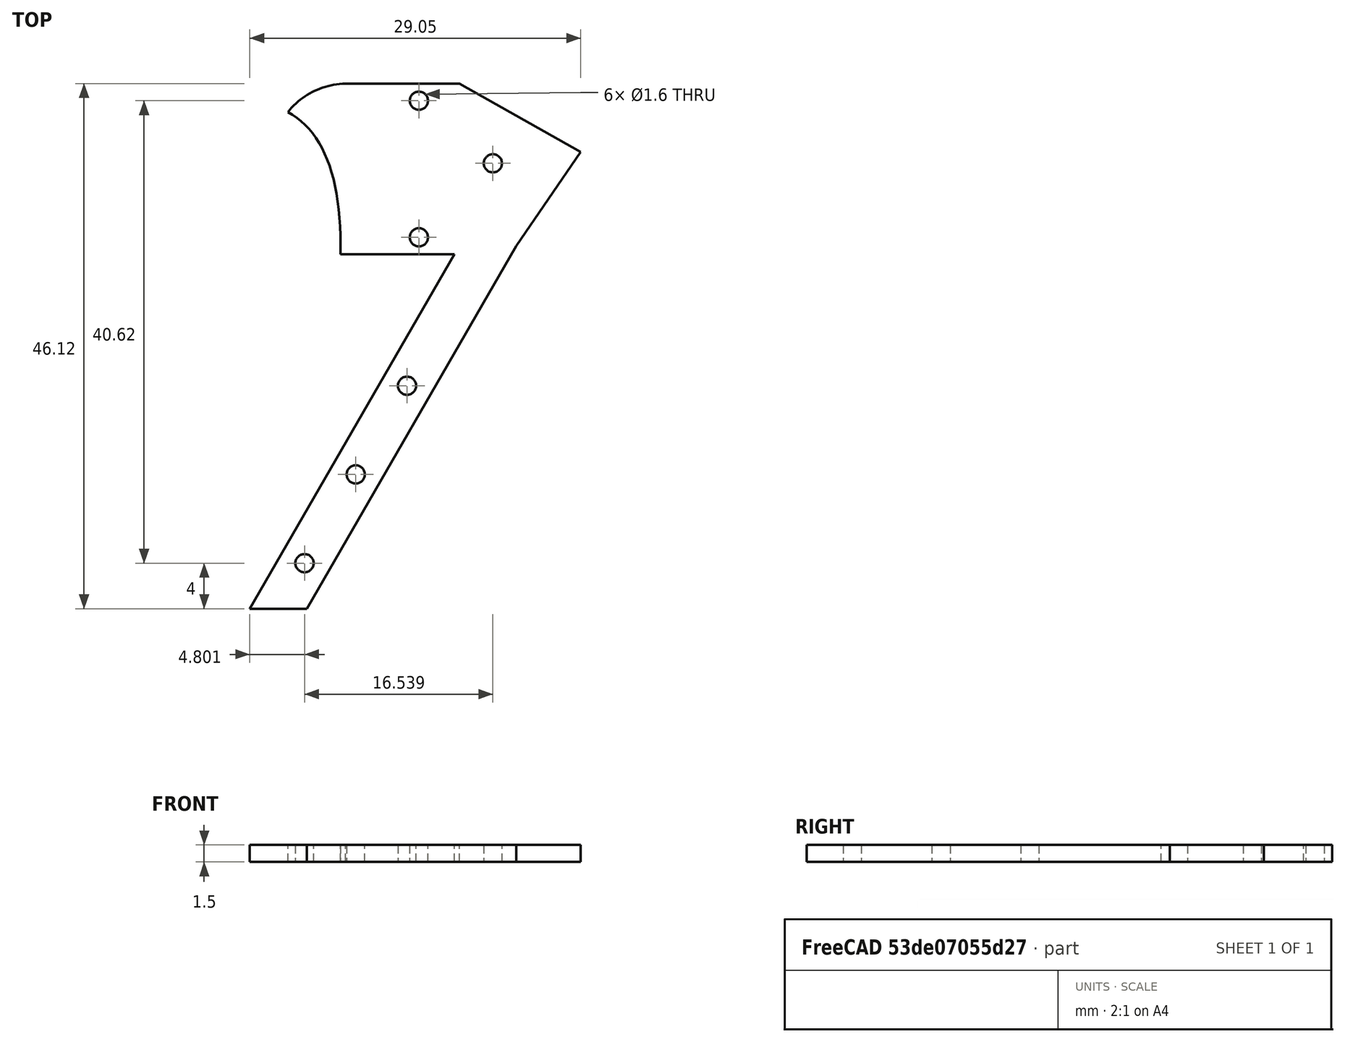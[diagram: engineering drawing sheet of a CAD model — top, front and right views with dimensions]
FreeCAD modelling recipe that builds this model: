
FCSTD DOCUMENT  (FreeCAD 0.17R13519 (Git))
Label: DingDengJia-jwei-2.0
License: All rights reserved
LicenseURL: http://en.wikipedia.org/wiki/All_rights_reserved
objects: Sketcher::SketchObject×1, PartDesign::Pad×1, PartDesign::Body×1
note: 4 computed .brp shape members not serialized (recipe doc carries the construction recipe); baked Part::Feature solids carry a one-line shape summary decoded from their .brp

FEATURE [Sketcher::SketchObject] Sketch
  MapMode = 5
  Support = -> [XY_Plane]
  sketch-geometry (25):
    g0: LineSegment StartX=12.1244 StartY=21 StartZ=0 EndX=2.12436 EndY=21 EndZ=0
    g1: LineSegment StartX=17.5548 StartY=21.7455 StartZ=0 EndX=23.2123 EndY=29.9913 EndZ=0
    g2: LineSegment StartX=23.2123 StartY=29.9913 StartZ=0 EndX=12.5721 EndY=36 EndZ=0
    g3: LineSegment StartX=2.57207 StartY=36 StartZ=0 EndX=12.5721 EndY=36 EndZ=0
    g4: Circle [constr] CenterX=2.57207 CenterY=36 CenterZ=0 NormalX=0 NormalY=0 NormalZ=1 AngleXU=0 Radius=0.9
    g5: Circle [constr] CenterX=-0.563366 CenterY=35.8843 CenterZ=0 NormalX=0 NormalY=0 NormalZ=1 AngleXU=0 Radius=0.9
    g6: Circle [constr] CenterX=-2.5 CenterY=33.5 CenterZ=0 NormalX=0 NormalY=0 NormalZ=1 AngleXU=0 Radius=0.9
    g7: BSplineCurve PolesCount=3 KnotsCount=2 Degree=2 IsPeriodic=0
    g8: GeomPoint [constr] X=2.57207 Y=36 Z=0
    g9: GeomPoint [constr] X=-2.5 Y=33.5 Z=0
    g10: Circle [constr] CenterX=-2.5 CenterY=33.5 CenterZ=0 NormalX=0 NormalY=0 NormalZ=1 AngleXU=0 Radius=0.7
    g11: Circle [constr] CenterX=2.30131 CenterY=30.8733 CenterZ=0 NormalX=0 NormalY=0 NormalZ=1 AngleXU=0 Radius=0.7
    g12: Circle [constr] CenterX=2.12436 CenterY=21 CenterZ=0 NormalX=0 NormalY=0 NormalZ=1 AngleXU=0 Radius=0.7
    g13: BSplineCurve PolesCount=3 KnotsCount=2 Degree=2 IsPeriodic=0
    g14: GeomPoint [constr] X=-2.5 Y=33.5 Z=0
    g15: GeomPoint [constr] X=2.12436 Y=21 Z=0
    g16: Circle CenterX=9 CenterY=22.5 CenterZ=0 NormalX=0 NormalY=0 NormalZ=1 AngleXU=0 Radius=0.8
    g17: Circle CenterX=9 CenterY=34.5 CenterZ=0 NormalX=0 NormalY=0 NormalZ=1 AngleXU=0 Radius=0.8
    g18: Circle CenterX=15.5 CenterY=29 CenterZ=0 NormalX=0 NormalY=0 NormalZ=1 AngleXU=0 Radius=0.8
    g19: Circle CenterX=-1.03921 CenterY=-6.11996 CenterZ=0 NormalX=0 NormalY=0 NormalZ=1 AngleXU=0 Radius=0.8
    g20: Circle CenterX=7.96079 CenterY=9.4685 CenterZ=0 NormalX=0 NormalY=0 NormalZ=1 AngleXU=0 Radius=0.8
    g21: LineSegment StartX=17.5548 StartY=21.7455 StartZ=0 EndX=-0.84276 EndY=-10.12 EndZ=0
    g22: LineSegment StartX=12.1244 StartY=21 StartZ=0 EndX=-5.84276 EndY=-10.12 EndZ=0
    g23: LineSegment StartX=-5.84276 StartY=-10.12 StartZ=0 EndX=-0.84276 EndY=-10.12 EndZ=0
    g24: Circle CenterX=3.46079 CenterY=1.67427 CenterZ=0 NormalX=0 NormalY=0 NormalZ=1 AngleXU=0 Radius=0.8
  constraints (54):
    c: Distance(g0) = 10
    c: Distance(g1) = 10
    c: Coincident(g2,g1)
    c: DistanceY(g0,g3) = 15
    c: Horizontal(g0)
    c: Horizontal(g3)
    c: DistanceX(g3,g3) = 10
    c: Coincident(g2,g3)
    c: Radius(g4) = 0.9
    c: Equal(g4,g5)
    c: Equal(g4,g6)
    c: InternalAlignment(g4,g7)
    c: InternalAlignment(g5,g7)
    c: InternalAlignment(g6,g7)
    c: InternalAlignment(g8,g7)
    c: InternalAlignment(g9,g7)
    c: Distance(g6,g3) = 2.5
    c: Coincident(g10,g6)
    c: Radius(g10) = 0.7
    c: Equal(g10,g11)
    c: Equal(g10,g12)
    c: Coincident(g12,g0)
    c: InternalAlignment(g10,g13)
    c: InternalAlignment(g11,g13)
    c: InternalAlignment(g12,g13)
    c: InternalAlignment(g14,g13)
    c: InternalAlignment(g15,g13)
    c: Radius(g16) = 0.8
    c: Radius(g17) = 0.8
    c: Distance(g17,g3) = 1.5
    c: Distance(g16,g0) = 1.5
    c: Radius(g18) = 0.8
    c: Distance(g18,g3) = 7
    c: Radius(g20) = 0.8
    c: Radius(g19) = 0.8
    c: DistanceY(g-1,g0) = 21
    c: Coincident(g4,g3)
    c: Angle(g2,g1) = 1.48353
    c: Coincident(g21,g1)
    c: Coincident(g22,g0)
    c: Coincident(g23,g22)
    c: Coincident(g23,g21)
    c: Horizontal(g23)
    c: DistanceX(g23,g23) = 5
    c: Angle(g23,g22) = 1.0472
    c: Angle(g21,g23) = 2.0944
    c: PointOnObject(g-1,g22)
    c: Radius(g24) = 0.8
    c: Distance(g19,g23) = 4
    c: Distance(g19,g22) = 2.16
    c: Distance(g24,g22) = 2.16
    c: Distance(g20,g22) = 2.16
    c: Distance(g24,g19) = 9
    c: Distance(g20,g24) = 9
FEATURE [PartDesign::Pad] Pad
  Length = 1.5
  Length2 = 100
  Profile = -> Sketch
  Type = 0
FEATURE [PartDesign::Body] Body
  Group = -> [Sketch,Pad]
  Origin = -> Origin
  Tip = -> Pad
